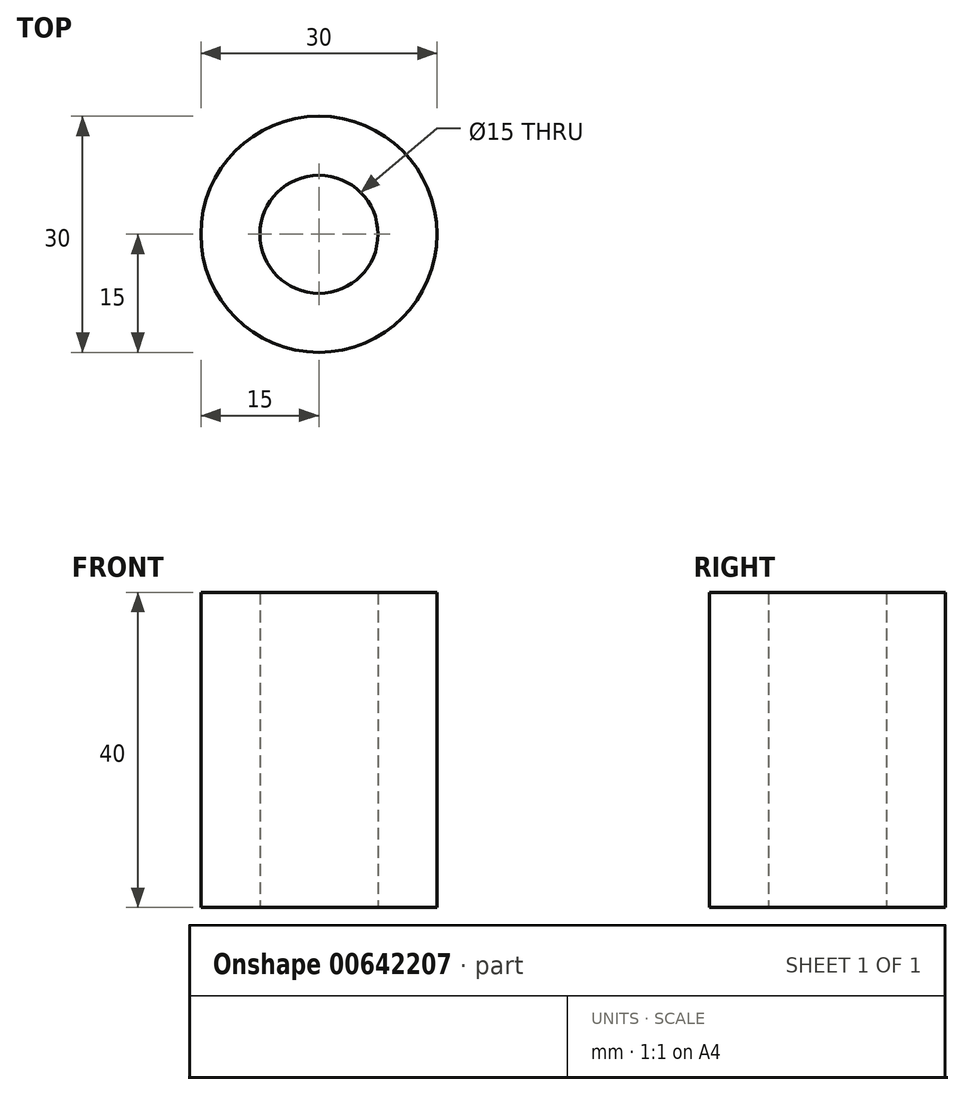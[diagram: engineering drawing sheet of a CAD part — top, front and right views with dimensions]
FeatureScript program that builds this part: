
annotation { "Feature Type Name" : "Feature", "Feature Type Description" : "" }
export const myFeature = defineFeature(function(context is Context, id is Id, definition is map)
    precondition{}
    {
        {
            var Q0;
            Q0=qCreatedBy(makeId("Top.planeOp"),FACE);
            var sketch = newSketch(context, id + "F0", { "sketchPlane" : qUnion([Q0])});
            skCircle(sketch, "E0", {"center": v(0, 0) * mm, "radius": 15 * mm});
            skCircle(sketch, "E1", {"center": v(0, 0) * mm, "radius": 7.5 * mm});
            skSolve(sketch);
        }
        {
            var Q0;
            Q0 = qSketchRegion(id + "F0", true);
            extrude(context, id + "F1", {"entities" : qUnion([Q0]), "depth" : 40 * mm, "offsetDistance" : 25 * mm});
        }
    });
